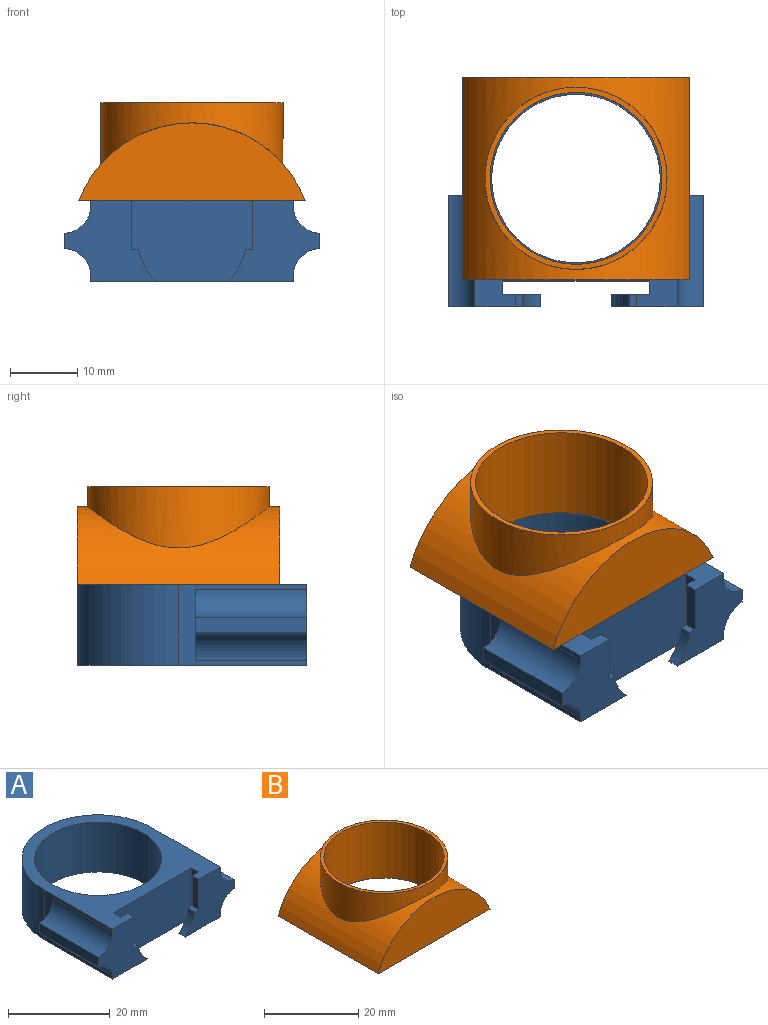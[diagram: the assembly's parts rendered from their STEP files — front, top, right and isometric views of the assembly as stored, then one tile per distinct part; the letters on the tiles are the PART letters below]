
ASSEMBLY  parts=2 mates=1
PART A: 27 faces, bbox 37.7x34x12 mm
  f0: plane 19x12mm, normal (-1,0,0), area 55mm2, adj f2,f3,f7,f8,f22,f25,f26
  f1: plane 19x12mm, normal (1,0,0), area 55mm2, adj f2,f3,f4,f7,f20,f23,f24
  f2: plane 34x30mm, normal (0,0,1), area 356.7mm2, adj f0,f1,f4,f5,f6,f7,f8,f9
  f3: plane 34x30mm, normal (0,0,-1), area 370.1mm2, adj f0,f1,f4,f5,f6,f7,f8,f9
  f4: plane 13.56x12mm, normal (0,-1,0), area 97.7mm2, adj f1,f2,f3,f13,f14,f15,f19,f23
  f5: plane 12x5.57mm, normal (0,1,0), area 32mm2, adj f2,f3,f9,f16,f17,f18
  f6: plane 12x5.57mm, normal (0,1,0), area 32mm2, adj f2,f3,f10,f13,f14,f15
  f7: cylinder r=15mm len=30mm, axis (0,0,-1), area 565.5mm2, adj f0,f1,f2,f3
  f8: plane 13.56x12mm, normal (0,-1,0), area 97.7mm2, adj f0,f2,f3,f16,f17,f18,f21,f25
  f9: plane 12x2mm, normal (1,0,0), area 24mm2, adj f2,f3,f5,f11
  f10: plane 12x2mm, normal (-1,0,0), area 24mm2, adj f2,f3,f6,f11
  f11: plane 21.72x12mm, normal (0,-1,0), area 260.6mm2, adj f2,f3,f9,f10
  f12: cylinder r=12.5mm len=25mm, axis (0,0,1), area 942.5mm2, adj f2,f3
  f13: plane 1.8x1.1mm, normal (0,0,1), area 2mm2, adj f4,f6,f14,f15
  f14: plane 7.25x1.8mm, normal (-1,0,0), area 13mm2, adj f2,f4,f6,f13
  f15: cylinder r=8mm len=4.75mm, axis (0,-1,0), area 10mm2, adj f3,f4,f6,f13
  f16: plane 7.25x1.8mm, normal (1,0,0), area 13mm2, adj f2,f5,f8,f18
  f17: cylinder r=8mm len=4.75mm, axis (0,-1,0), area 10mm2, adj f3,f5,f8,f18
  f18: plane 1.8x1.1mm, normal (0,0,1), area 2mm2, adj f5,f8,f16,f17
  f19: plane 16.5x2.3mm, normal (1,0,0), area 37.9mm2, adj f4,f20,f23,f24
  f20: plane 10.48x3.85mm, normal (0,1,0), area 16mm2, adj f1,f19,f23,f24
  f21: plane 16.5x2.3mm, normal (-1,0,0), area 37.9mm2, adj f8,f22,f25,f26
  f22: plane 10.48x3.85mm, normal (0,1,0), area 16mm2, adj f0,f21,f25,f26
  f23: cylinder r=4.1mm len=16.5mm, axis (0,1,0), area 102.1mm2, adj f1,f4,f19,f20
  f24: cylinder r=4.1mm len=16.5mm, axis (0,1,0), area 102.1mm2, adj f1,f4,f19,f20
  f25: cylinder r=4.1mm len=16.5mm, axis (0,1,0), area 102.1mm2, adj f0,f8,f21,f22
  f26: cylinder r=4.1mm len=16.5mm, axis (0,1,0), area 102.1mm2, adj f0,f8,f21,f22
PART B: 7 faces, bbox 33.6x30x14.5 mm
  f0: cylinder r=18mm len=33.57mm, axis (0,-1,0), area 672.2mm2, adj f1,f2,f3,f4
  f1: plane 33.57x30mm, normal (0,0,-1), area 496.4mm2, adj f0,f2,f3,f6
  f2: plane 33.57x11.5mm, normal (0,1,0), area 280.1mm2, adj f0,f1
  f3: plane 33.57x11.5mm, normal (0,-1,0), area 280.1mm2, adj f0,f1
  f4: cylinder r=13.5mm len=27mm, axis (0,0,-1), area 499.4mm2, adj f0,f5
  f5: plane 27x27mm, normal (0,0,1), area 61.9mm2, adj f4,f6
  f6: cylinder r=12.75mm len=25.5mm, axis (0,0,-1), area 1161.6mm2, adj f1,f5
PLACE A t=(0.1,-17.65,-5.71)mm
PLACE B t=(0.1,-32.65,0.29)mm
MATE planar B.f1 <-> A.f2  axis (0,0,-1) through (0.1,-2.65,0.29)mm
